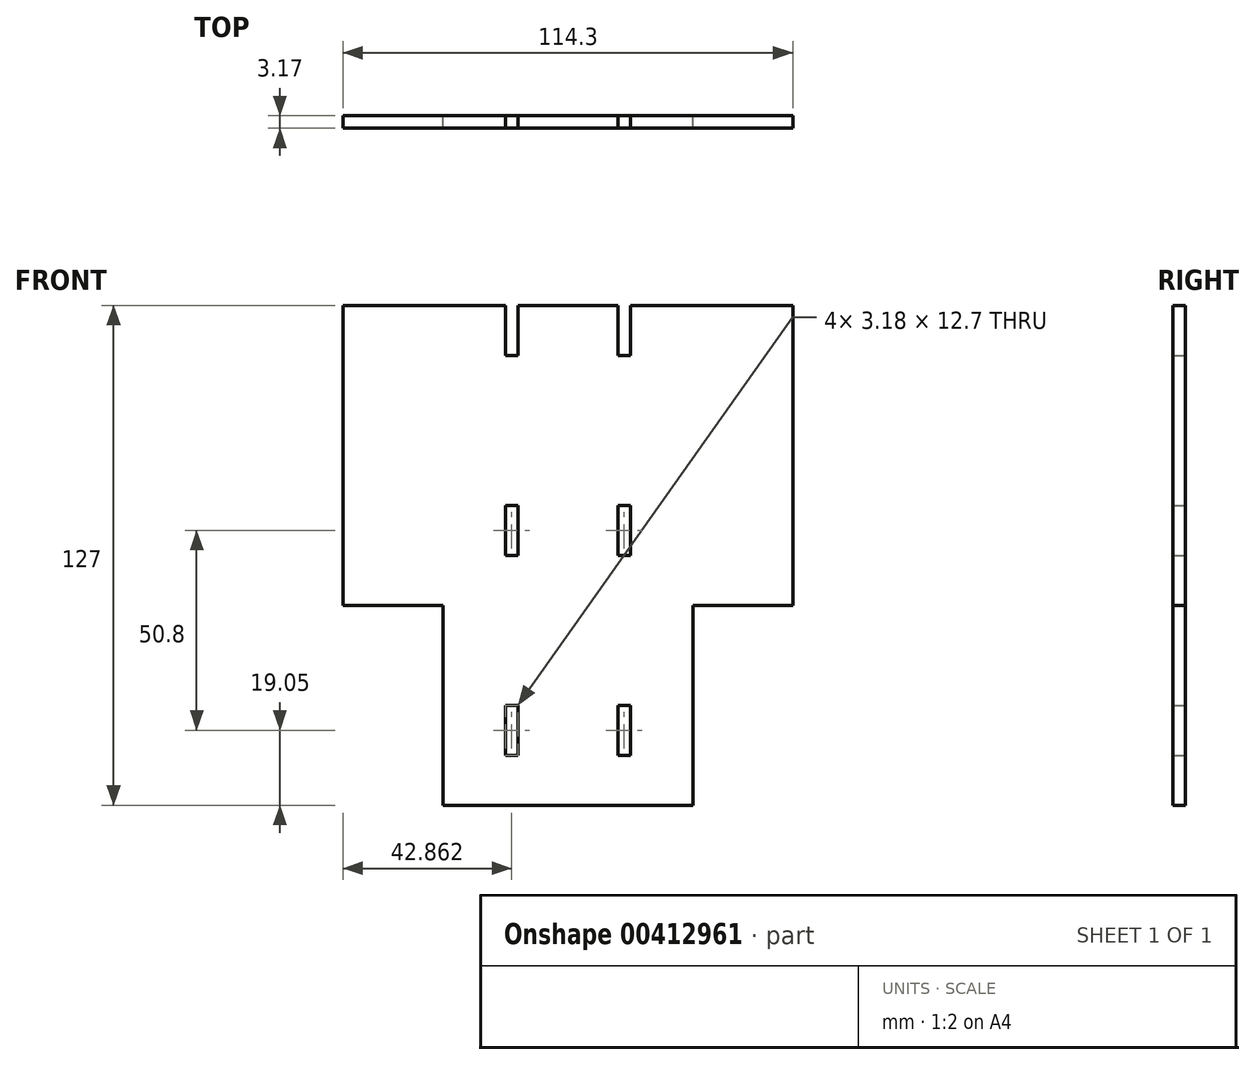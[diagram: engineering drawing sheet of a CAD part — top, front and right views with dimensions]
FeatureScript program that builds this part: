
annotation { "Feature Type Name" : "Feature", "Feature Type Description" : "" }
export const myFeature = defineFeature(function(context is Context, id is Id, definition is map)
    precondition{}
    {
        {
            var Q0;
            Q0=qCreatedBy(makeId("Front.planeOp"),FACE);
            var sketch = newSketch(context, id + "F0", { "sketchPlane" : qUnion([Q0])});
            skLineSegment(sketch, "E0.bottom", {"start": v(57.15, 63.5) * mm, "end": v(15.87, 63.5) * mm});
            skLineSegment(sketch, "E0.top", {"start": v(0, -63.5) * mm, "end": v(-31.75, -63.5) * mm});
            skLineSegment(sketch, "E0.left", {"start": v(57.15, 63.5) * mm, "end": v(57.15, -12.7) * mm});
            skLineSegment(sketch, "E0.right", {"start": v(-57.15, 63.5) * mm, "end": v(-57.15, -12.7) * mm});
            skPoint(sketch, "E0.middle", {"position": v(0, 0) * mm});
            skLineSegment(sketch, "E1", {"start": v(-31.75, -38.1) * mm, "end": v(-31.75, -12.7) * mm});
            skLineSegment(sketch, "E2", {"start": v(-31.75, -12.7) * mm, "end": v(-57.15, -12.7) * mm});
            skLineSegment(sketch, "E3.MirrorCS", {"start": v(31.75, -12.7) * mm, "end": v(57.15, -12.7) * mm});
            skLineSegment(sketch, "E4.MirrorCS", {"start": v(31.75, -38.1) * mm, "end": v(31.75, -12.7) * mm});
            skLineSegment(sketch, "E5", {"start": v(0, 0) * mm, "end": v(0, 63.5) * mm});
            skLineSegment(sketch, "E6", {"start": v(0, 0) * mm, "end": v(0, -63.5) * mm});
            skLineSegment(sketch, "E7.bottom", {"start": v(-15.87, 0) * mm, "end": v(-12.7, 0) * mm});
            skLineSegment(sketch, "E7.top", {"start": v(-15.88, 12.7) * mm, "end": v(-12.7, 12.7) * mm});
            skLineSegment(sketch, "E7.left", {"start": v(-15.87, 0) * mm, "end": v(-15.87, 12.7) * mm});
            skLineSegment(sketch, "E7.right", {"start": v(-12.7, 0) * mm, "end": v(-12.7, 12.7) * mm});
            skLineSegment(sketch, "E8.bottom", {"start": v(-15.87, -50.8) * mm, "end": v(-12.7, -50.8) * mm});
            skLineSegment(sketch, "E8.top", {"start": v(-15.87, -38.1) * mm, "end": v(-12.7, -38.1) * mm});
            skLineSegment(sketch, "E8.left", {"start": v(-15.87, -50.8) * mm, "end": v(-15.87, -38.1) * mm});
            skLineSegment(sketch, "E8.right", {"start": v(-12.7, -50.8) * mm, "end": v(-12.7, -38.1) * mm});
            skLineSegment(sketch, "E9.MirrorCS", {"start": v(15.87, 0) * mm, "end": v(15.87, 12.7) * mm});
            skLineSegment(sketch, "E10.MirrorCS", {"start": v(15.88, 12.7) * mm, "end": v(12.7, 12.7) * mm});
            skLineSegment(sketch, "E11.MirrorCS", {"start": v(12.7, 0) * mm, "end": v(12.7, 12.7) * mm});
            skLineSegment(sketch, "E12.MirrorCS", {"start": v(15.88, 0) * mm, "end": v(12.7, 0) * mm});
            skLineSegment(sketch, "E13.MirrorCS", {"start": v(12.7, -50.8) * mm, "end": v(12.7, -38.1) * mm});
            skLineSegment(sketch, "E14.MirrorCS", {"start": v(15.88, -38.1) * mm, "end": v(12.7, -38.1) * mm});
            skLineSegment(sketch, "E15.MirrorCS", {"start": v(15.88, -50.8) * mm, "end": v(15.88, -38.1) * mm});
            skLineSegment(sketch, "E16.MirrorCS", {"start": v(15.88, -50.8) * mm, "end": v(12.7, -50.8) * mm});
            skLineSegment(sketch, "E17", {"start": v(-12.7, 63.5) * mm, "end": v(-12.7, 50.8) * mm});
            skLineSegment(sketch, "E18", {"start": v(-12.7, 50.8) * mm, "end": v(-15.88, 50.8) * mm});
            skLineSegment(sketch, "E19", {"start": v(-15.88, 50.8) * mm, "end": v(-15.88, 63.5) * mm});
            skLineSegment(sketch, "E20.MirrorCS", {"start": v(12.7, 63.5) * mm, "end": v(12.7, 50.8) * mm});
            skLineSegment(sketch, "E21.MirrorCS", {"start": v(15.87, 50.8) * mm, "end": v(15.87, 63.5) * mm});
            skLineSegment(sketch, "E22.MirrorCS", {"start": v(12.7, 50.8) * mm, "end": v(15.87, 50.8) * mm});
            skLineSegment(sketch, "E23.trimOffspring", {"start": v(-15.88, 63.5) * mm, "end": v(-57.15, 63.5) * mm});
            skLineSegment(sketch, "E24.trimOffspring", {"start": v(12.7, 63.5) * mm, "end": v(-12.7, 63.5) * mm});
            skLineSegment(sketch, "E25", {"start": v(-31.75, -38.1) * mm, "end": v(-31.75, -63.5) * mm});
            skLineSegment(sketch, "E26", {"start": v(31.75, -38.1) * mm, "end": v(31.75, -63.5) * mm});
            skPoint(sketch, "E27.trimOffspring.start.orphan", {"position": v(-57.15, -38.1) * mm});
            skPoint(sketch, "E28.orphan", {"position": v(-57.15, -63.5) * mm});
            skPoint(sketch, "E29.trimOffspring.end.orphan", {"position": v(57.15, -63.5) * mm});
            skPoint(sketch, "E30.MirrorCS.end.orphan", {"position": v(31.75, -38.1) * mm});
            skPoint(sketch, "E30.MirrorCS.start.orphan", {"position": v(57.15, -38.1) * mm});
            skLineSegment(sketch, "E31", {"start": v(0, -63.5) * mm, "end": v(31.75, -63.5) * mm});
            skSolve(sketch);
        }
        {
            var Q0;
            Q0 = qSketchRegion(id + "F0", true);
            extrude(context, id + "F1", {"entities" : qUnion([Q0]), "depth" : 3.17 * mm});
        }
    });
